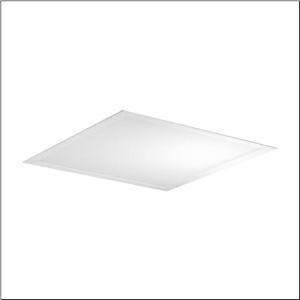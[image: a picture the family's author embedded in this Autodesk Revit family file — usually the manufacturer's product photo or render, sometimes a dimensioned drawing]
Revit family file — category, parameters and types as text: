
# Revit family: apollon_r__21_square_51mq11w72314_ea86
name_source: partatom
category: Lighting Fixtures
units: mm (PartAtom-declared; Revit-internal decimal feet)

## family parameters
Cut with Voids When Loaded = No
Host = Face
Light Source = No
Part Type = Normal
Room Calculation Point = No
Round Connector Dimension = Use Diameter
Shared = No

## types (1)
- Apollon® 21 square (1 x LED, 4100 lm, 23.3 W, 3000K)
    Apparent Load = 23 VA
    CIE Flux Codes = 60 87 97 100 100
    Color Rendering = 80
    Color Temperature = 3000K
    Default Elevation = 1800 mm
    Description = Apollon® 21 square, office luminaire, primary optical cover: micro prismatic cover, of PMMA, CAT 2 (L<= 3000cd/m²), light emission: direct distribution, primary light characteristic: symmetric, installation type: lay-in mounting, LED, rated luminous flux: 4.100lm, luminous efficacy: 176lm/W, light colour: 830, colour temperature: 3000K, with terminal, 3-pole, mains connection: 220..240V, AC/DC, 0/50..60Hz, rated input power: 23.3W, housing, of aluminium, coated, traffic white (RAL 9016), module: M625, length: 620mm, width: 620mm, height: 30mm, housing upper side, of sheet steel, galvanised, protection rating (complete): IP20, protection rating (lamp compartment, on room side): IP50, insulation class (complete): insulation class II (safety insulation), certification: CE, ENEC, impact resistance: IK03, permissible operating ambient temperature: -20..+45°C, permissible storage temperature: -40..+80°C, packaging unit: 1 piece
    Height = 0 mm  [stored 0 ft]
    Lamp = 1 x LED
    Lamp Light Flux = 4100 lm
    Lamp Power = 23.3 W
    Lamp count = 1
    Length = 620 mm
    Luminous efficacy = 176 lm/W
    Manufacturer = Siteco
    ModVariant = No
    Model = 51MQ11W72314
    Mounting Place = Ceiling
    Mounting Type = Recessed
    Number of Poles = 1
    OnlyDefault = Yes
    Power Factor = 1
    Product Name = Apollon® 21 square
    Product group = office luminaire | ceiling recessed
    ProductGroupID = 400
    Protection Class = Protection class II
    Protection Degree = IP 20
    RLX_Detail_Level = 1
    RLX_Emergency_Light_Flux = 0 lm
    RLX_Emergency_Type = 0
    RLX_Emergency_Type_DB = No
    RlxData = <blob elided: 12945 chars, md5=ebf79043>
    Socket = socket
    Standby Power = 0 W
    System Light Flux = 4100 lm
    System Power = 23 W
    Type Comments = Product without accessories
    Type Image = l_1291054.jpg
    URL = http://relux.com
    VarID = ---
    Voltage = 0 V
    Weight = 0.00 kg
    Width = 620 mm

note: [stored X ft] marks values corroborated as IEEE doubles in the binary element streams (Revit-internal decimal feet)

## geometry (parser evidence)
native form markers: Sweep x10
no freeform markers — native parametric forms only
